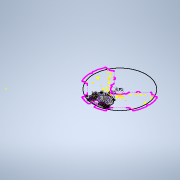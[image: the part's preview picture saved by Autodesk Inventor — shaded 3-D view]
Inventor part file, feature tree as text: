
AUTODESK INVENTOR PART (.ipt)
format: ipt  version: 2020 (Build 240168000, 168)  size: 673,792 bytes
history: native  units: mm
features: extrude x4, sketch x3, other x2, projected_geometry x2, chamfer x1, fillet x1
ambient origin geometry x8: Origin, YZ Plane, XZ Plane, XY Plane, X Axis, Y Axis, Z Axis, Center Point
bodies: Body1 (feature_tree)
feature tree (13):
  other  "Твердое тело1"
  other  "РабПлоскость1"
  sketch  "Эскиз1"
  extrude  "Выдавливание1"  Depth=3.0mm
  extrude  "Выдавливание2"  Depth=7.0mm
  chamfer  "Фаска1"  Distance=4.75mm
  fillet  "Сопряжение1"  Radius=4.75mm
  sketch  "Эскиз2"
  extrude  "Выдавливание3"  Depth=1.0mm
  extrude  "Выдавливание4"  Depth=1.0mm
  projected_geometry  "Спроецированная петля1"
  projected_geometry  "Спроецированная петля18"
  sketch  "Эскиз3"
